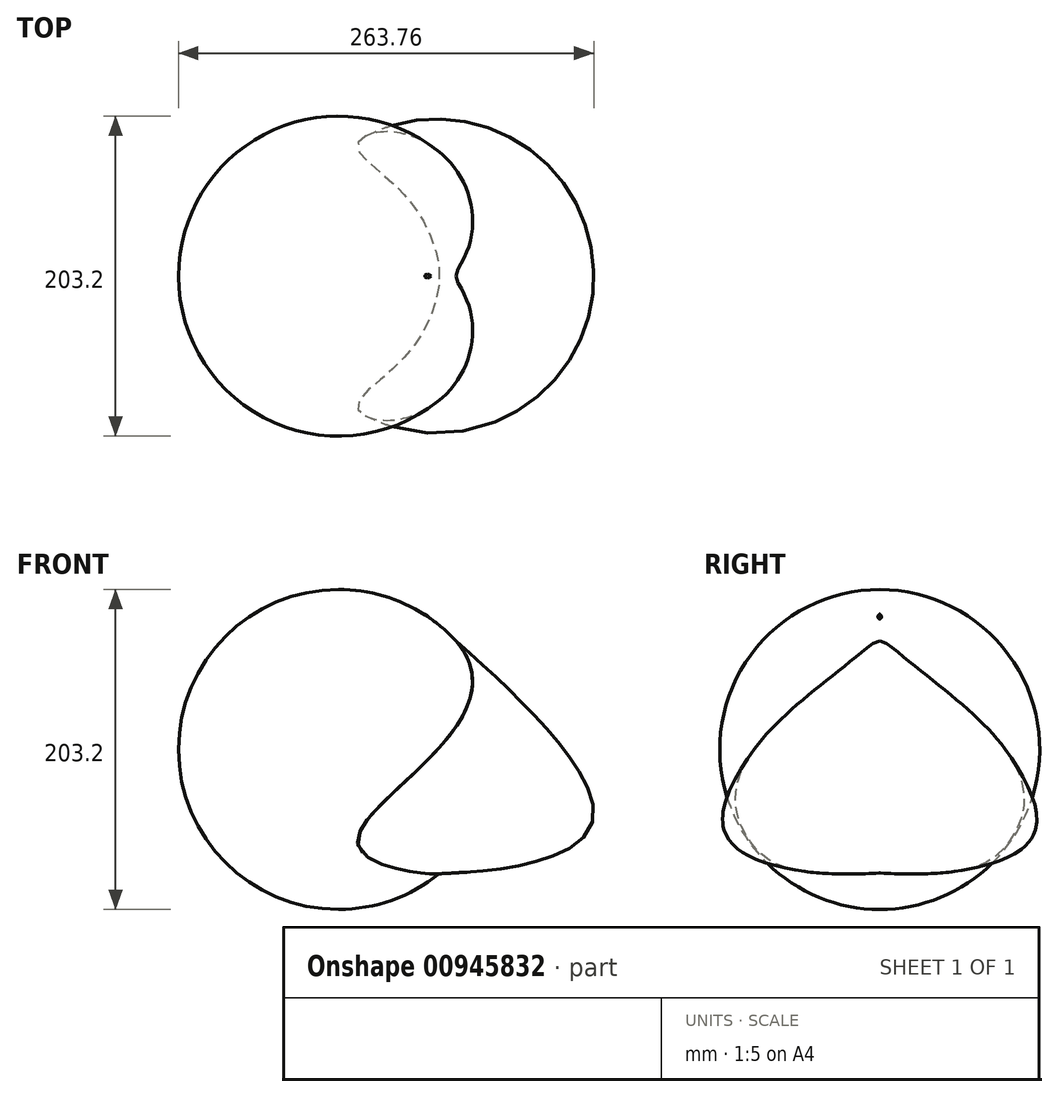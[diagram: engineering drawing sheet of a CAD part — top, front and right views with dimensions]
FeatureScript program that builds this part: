
annotation { "Feature Type Name" : "Feature", "Feature Type Description" : "" }
export const myFeature = defineFeature(function(context is Context, id is Id, definition is map)
    precondition{}
    {
        {
            var Q0;
            Q0=qCreatedBy(makeId("Right.planeOp"),FACE);
            var sketch = newSketch(context, id + "F0", { "sketchPlane" : qUnion([Q0])});
            skArc(sketch, "E0", {"start": v(0, -101.6) * mm, "mid": v(101.6, 0) * mm, "end": v(0, 101.6) * mm});
            skLineSegment(sketch, "E1", {"start": v(0, 101.6) * mm, "end": v(0, -101.6) * mm});
            skSolve(sketch);
        }
        {
            var Q0;
            Q0=makeQuery(id+"F0.imprint","IMPRINT",FACE,{"disambiguationData":[TD([[makeQuery(id+"F0.imprint","IMPRINT",EDGE,{"derivedFrom":sQuery(id+"F0.wireOp",EDGE,"E0")}),1.0]])]});
            var Q1;
            Q1=sQuery(id+"F0.wireOp",EDGE,"E1");
            revolve(context, id + "F1", {"surfaceOperationType" : NewSurfaceOperationType.NEW, "entities" : qUnion([Q0]), "axis" : qUnion([Q1]), "revolveType" : RevolveType.FULL});
        }
        {
            var Q0;
            Q0=qCreatedBy(makeId("Front.planeOp"),FACE);
            var sketch = newSketch(context, id + "F2", { "sketchPlane" : qUnion([Q0])});
            skFitSpline(sketch, "E2", {"points": [v(55.2, 85.97) * mm, v(161.09, -47.3) * mm, v(64.37, -78.46) * mm], "startDerivative": vector(235.53, -205.23) * mm, "endDerivative": vector(-210.27, 1.96) * mm});
            skLineSegment(sketch, "E3", {"start": v(55.2, 85.97) * mm, "end": v(64.37, -78.46) * mm});
            skSolve(sketch);
        }
        {
            var Q0;
            Q0=makeQuery(id+"F2.imprint","IMPRINT",FACE,{"disambiguationData":[TD([[makeQuery(id+"F2.imprint","IMPRINT",EDGE,{"derivedFrom":sQuery(id+"F2.wireOp",EDGE,"E2")}),-1.0]])]});
            var Q1;
            Q1=sQuery(id+"F2.wireOp",EDGE,"E3");
            revolve(context, id + "F3", {"operationType" : NewBodyOperationType.ADD, "surfaceOperationType" : NewSurfaceOperationType.NEW, "entities" : qUnion([Q0]), "axis" : qUnion([Q1]), "revolveType" : RevolveType.FULL});
        }
    });
